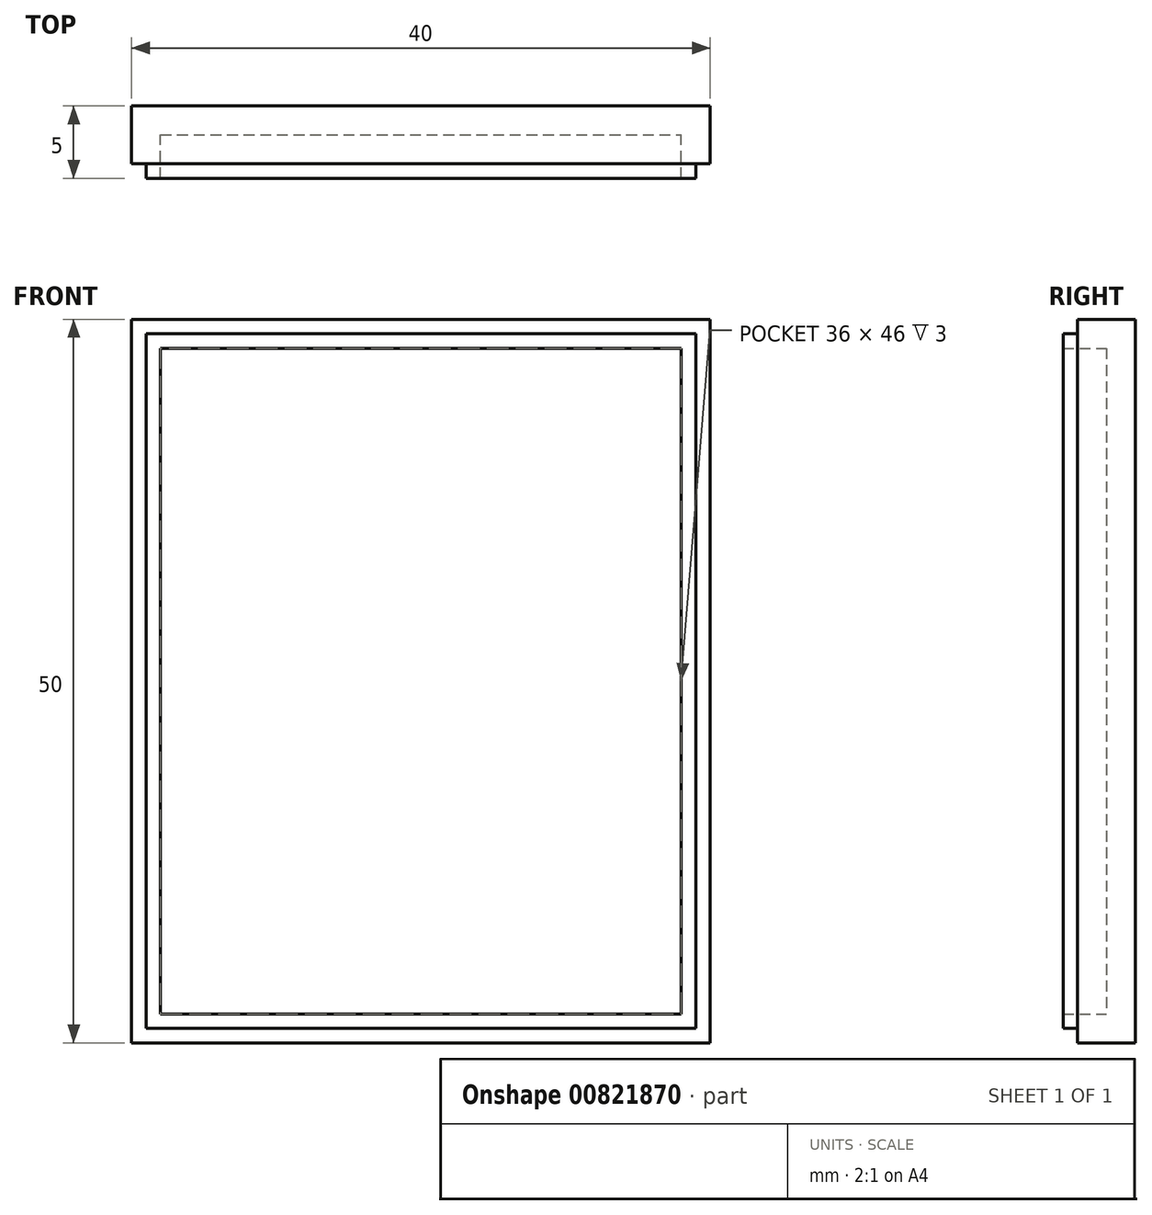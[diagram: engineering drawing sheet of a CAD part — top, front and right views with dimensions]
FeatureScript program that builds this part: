
annotation { "Feature Type Name" : "Feature", "Feature Type Description" : "" }
export const myFeature = defineFeature(function(context is Context, id is Id, definition is map)
    precondition{}
    {
        {
            var Q0;
            Q0=qCreatedBy(makeId("Front.planeOp"),FACE);
            var sketch = newSketch(context, id + "F0", { "sketchPlane" : qUnion([Q0])});
            skLineSegment(sketch, "E0.bottom", {"start": v(-20, 25) * mm, "end": v(20, 25) * mm});
            skLineSegment(sketch, "E0.top", {"start": v(-20, -25) * mm, "end": v(20, -25) * mm});
            skLineSegment(sketch, "E0.left", {"start": v(-20, 25) * mm, "end": v(-20, -25) * mm});
            skLineSegment(sketch, "E0.right", {"start": v(20, 25) * mm, "end": v(20, -25) * mm});
            skPoint(sketch, "E0.middle", {"position": v(0, 0) * mm});
            skSolve(sketch);
        }
        {
            var Q0;
            Q0=makeQuery(id+"F0.imprint","IMPRINT",FACE,{"disambiguationData":[TD([[makeQuery(id+"F0.imprint","IMPRINT",EDGE,{"derivedFrom":sQuery(id+"F0.wireOp",EDGE,"E0.bottom")}),-1.0]])]});
            extrude(context, id + "F1", {"entities" : qUnion([Q0]), "depth" : 2 * mm, "offsetDistance" : 25 * mm});
        }
        {
            var Q0;
            Q0=makeQuery(id+"F1.opExtrude","CAP_FACE",FACE,{"disambiguationData":[OSD([sQuery(id+"F0.wireOp",EDGE,"E0.bottom"),sQuery(id+"F0.wireOp",EDGE,"E0.top"),sQuery(id+"F0.wireOp",EDGE,"E0.left"),sQuery(id+"F0.wireOp",EDGE,"E0.right")])],"isStart":false});
            var sketch = newSketch(context, id + "F2", { "sketchPlane" : qUnion([Q0])});
            skLineSegment(sketch, "E1.bottom", {"start": v(-18, 23) * mm, "end": v(18, 23) * mm});
            skLineSegment(sketch, "E1.top", {"start": v(-18, -23) * mm, "end": v(18, -23) * mm});
            skLineSegment(sketch, "E1.left", {"start": v(-18, 23) * mm, "end": v(-18, -23) * mm});
            skLineSegment(sketch, "E1.right", {"start": v(18, 23) * mm, "end": v(18, -23) * mm});
            skPoint(sketch, "E1.middle", {"position": v(0, 0) * mm});
            skSolve(sketch);
        }
        {
            var Q0;
            Q0=makeQuery(id+"F2.imprint","IMPRINT",FACE,{"disambiguationData":[TD([[makeQuery(id+"F2.imprint","IMPRINT",EDGE,{"derivedFrom":sQuery(id+"F2.wireOp",EDGE,"E1.bottom")}),1.0]])]});
            extrude(context, id + "F3", {"entities" : qUnion([Q0]), "operationType" : NewBodyOperationType.ADD, "depth" : 2 * mm, "offsetDistance" : 25 * mm});
        }
        {
            var Q0;
            Q0=makeQuery(id+"F3.opExtrude","CAP_FACE",FACE,{"disambiguationData":[OSD([sQuery(id+"F0.wireOp",EDGE,"E0.bottom"),sQuery(id+"F0.wireOp",EDGE,"E0.top"),sQuery(id+"F0.wireOp",EDGE,"E0.left"),sQuery(id+"F0.wireOp",EDGE,"E0.right"),sQuery(id+"F2.wireOp",EDGE,"E1.bottom"),sQuery(id+"F2.wireOp",EDGE,"E1.top"),sQuery(id+"F2.wireOp",EDGE,"E1.left"),sQuery(id+"F2.wireOp",EDGE,"E1.right")])],"isStart":false});
            var sketch = newSketch(context, id + "F4", { "sketchPlane" : qUnion([Q0])});
            skLineSegment(sketch, "E2.bottom", {"start": v(-19, 24) * mm, "end": v(19, 24) * mm});
            skLineSegment(sketch, "E2.top", {"start": v(-19, -24) * mm, "end": v(19, -24) * mm});
            skLineSegment(sketch, "E2.left", {"start": v(-19, 24) * mm, "end": v(-19, -24) * mm});
            skLineSegment(sketch, "E2.right", {"start": v(19, 24) * mm, "end": v(19, -24) * mm});
            skPoint(sketch, "E2.middle", {"position": v(0, 0) * mm});
            skLineSegment(sketch, "E3.0", {"start": v(-18, 23) * mm, "end": v(-18, -23) * mm});
            skLineSegment(sketch, "E3.1", {"start": v(-18, 23) * mm, "end": v(18, 23) * mm});
            skLineSegment(sketch, "E3.2", {"start": v(18, 23) * mm, "end": v(18, -23) * mm});
            skLineSegment(sketch, "E3.3", {"start": v(-18, -23) * mm, "end": v(18, -23) * mm});
            skSolve(sketch);
        }
        {
            var Q0;
            Q0=makeQuery(id+"F4.imprint","IMPRINT",FACE,{"disambiguationData":[TD([[makeQuery(id+"F4.imprint","IMPRINT",EDGE,{"derivedFrom":sQuery(id+"F4.wireOp",EDGE,"E2.bottom")}),-1.0]])]});
            extrude(context, id + "F5", {"entities" : qUnion([Q0]), "operationType" : NewBodyOperationType.ADD, "depth" : 1 * mm, "offsetDistance" : 25 * mm});
        }
    });
